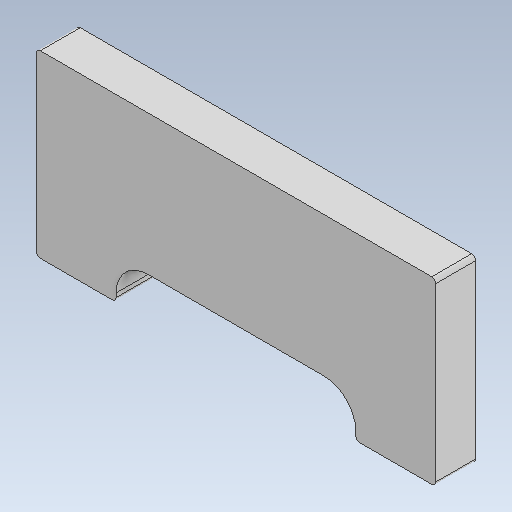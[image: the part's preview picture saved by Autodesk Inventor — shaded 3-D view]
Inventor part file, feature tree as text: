
AUTODESK INVENTOR PART (.ipt)
format: ipt  version: 2020 (Build 240168000, 168)  size: 106,496 bytes
history: native  units: mm
features: other x3, sketch x1
ambient origin geometry x8: Origin, YZ Plane, XZ Plane, XY Plane, X Axis, Y Axis, Z Axis, Center Point
bodies: Solid1 (feature_tree)
feature tree (4):
  other  "SlipersLåda 211018008.ipt"
  other  "Solid1::SlipersLåda 211018008.ipt"
  other  "TaggingFeature1"
  sketch  "Sketch1"  dims[d0=10.0mm]
